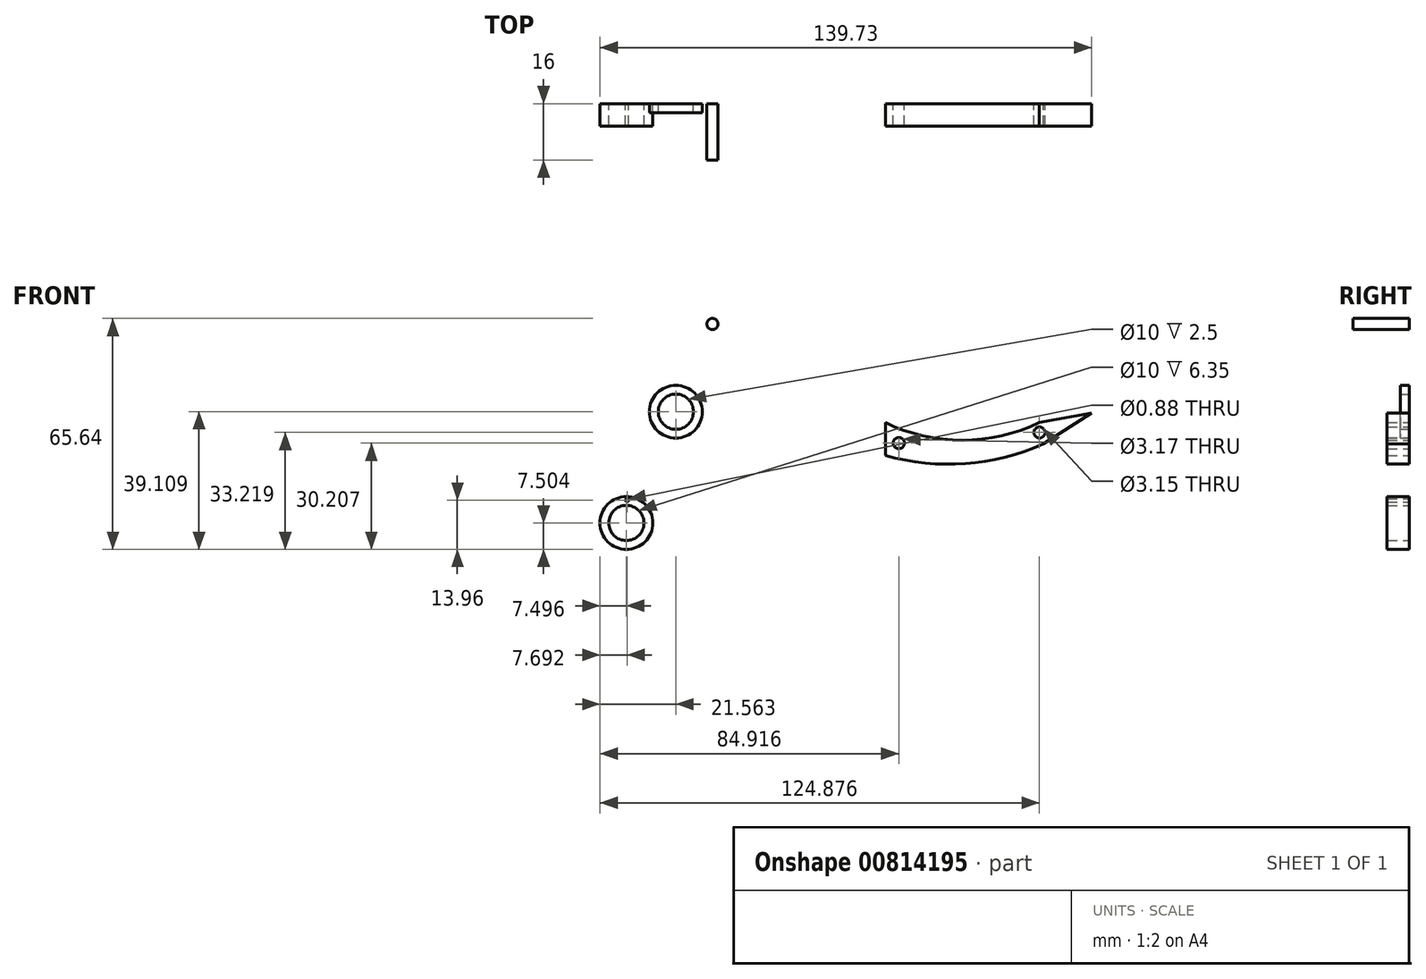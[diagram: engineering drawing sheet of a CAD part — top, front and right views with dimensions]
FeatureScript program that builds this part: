
annotation { "Feature Type Name" : "Feature", "Feature Type Description" : "" }
export const myFeature = defineFeature(function(context is Context, id is Id, definition is map)
    precondition{}
    {
        {
            var Q0;
            Q0=qCreatedBy(makeId("Front.planeOp"),FACE);
            var sketch = newSketch(context, id + "F0", { "sketchPlane" : qUnion([Q0])});
            skLineSegment(sketch, "E0", {"start": v(0, 0) * mm, "end": v(0, -9.37) * mm});
            skArc(sketch, "E1", {"start": v(0, -9.37) * mm, "mid": v(22.71, -11.63) * mm, "end": v(44.84, -6.05) * mm});
            skArc(sketch, "E2", {"start": v(0, 0) * mm, "mid": v(21.83, -4.98) * mm, "end": v(43.66, 0) * mm});
            skLineSegment(sketch, "E3", {"start": v(43.66, 0) * mm, "end": v(58.6, 2.73) * mm});
            skLineSegment(sketch, "E4", {"start": v(58.6, 2.73) * mm, "end": v(44.84, -6.05) * mm});
            skCircle(sketch, "E5", {"center": v(3.8, -5.81) * mm, "radius": 1.59 * mm});
            skCircle(sketch, "E6", {"center": v(-73.62, -28.52) * mm, "radius": 7.5 * mm});
            skCircle(sketch, "E7", {"center": v(-73.62, -28.52) * mm, "radius": 5 * mm});
            skCircle(sketch, "E8", {"center": v(-49.16, 28.03) * mm, "radius": 1.59 * mm});
            skCircle(sketch, "E9", {"center": v(-73.43, -22.06) * mm, "radius": 0.44 * mm});
            skCircle(sketch, "E10", {"center": v(43.76, -2.8) * mm, "radius": 1.58 * mm});
            skCircle(sketch, "E11", {"center": v(-59.56, 3.09) * mm, "radius": 7.5 * mm});
            skCircle(sketch, "E12", {"center": v(-59.56, 3.09) * mm, "radius": 5 * mm});
            skSolve(sketch);
        }
        {
            var Q0;
            Q0=makeQuery(id+"F0.imprint","IMPRINT",FACE,{"disambiguationData":[TD([[makeQuery(id+"F0.imprint","IMPRINT",EDGE,{"derivedFrom":sQuery(id+"F0.wireOp",EDGE,"E0")}),1.0]])]});
            extrude(context, id + "F1", {"entities" : qUnion([Q0]), "depth" : 6.35 * mm, "offsetDistance" : 25.4 * mm});
        }
        {
            var Q0;
            Q0=makeQuery(id+"F0.imprint","IMPRINT",FACE,{"disambiguationData":[TD([[makeQuery(id+"F0.imprint","IMPRINT",EDGE,{"derivedFrom":sQuery(id+"F0.wireOp",EDGE,"E8")}),1.0]])]});
            var Q1;
            Q1=makeQuery(id+"F0.imprint","IMPRINT",FACE,{"disambiguationData":[TD([[makeQuery(id+"F0.imprint","IMPRINT",EDGE,{"derivedFrom":sQuery(id+"F0.wireOp",EDGE,"E6")}),1.0]])]});
            extrude(context, id + "F2", {"entities" : qUnion([Q0, Q1]), "depth" : 6.35 * mm, "offsetDistance" : 25.4 * mm});
        }
        {
            var Q0;
            Q0=makeQuery(id+"F0.imprint","IMPRINT",FACE,{"disambiguationData":[TD([[makeQuery(id+"F0.imprint","IMPRINT",EDGE,{"derivedFrom":sQuery(id+"F0.wireOp",EDGE,"E8")}),1.0]])]});
            extrude(context, id + "F3", {"entities" : qUnion([Q0]), "operationType" : NewBodyOperationType.ADD, "depth" : 16 * mm, "offsetDistance" : 25.4 * mm});
        }
        {
            var Q0;
            Q0=makeQuery(id+"F0.imprint","IMPRINT",FACE,{"disambiguationData":[TD([[makeQuery(id+"F0.imprint","IMPRINT",EDGE,{"derivedFrom":sQuery(id+"F0.wireOp",EDGE,"E11")}),1.0]])]});
            extrude(context, id + "F4", {"entities" : qUnion([Q0]), "depth" : 2.5 * mm, "offsetDistance" : 25 * mm});
        }
    });
